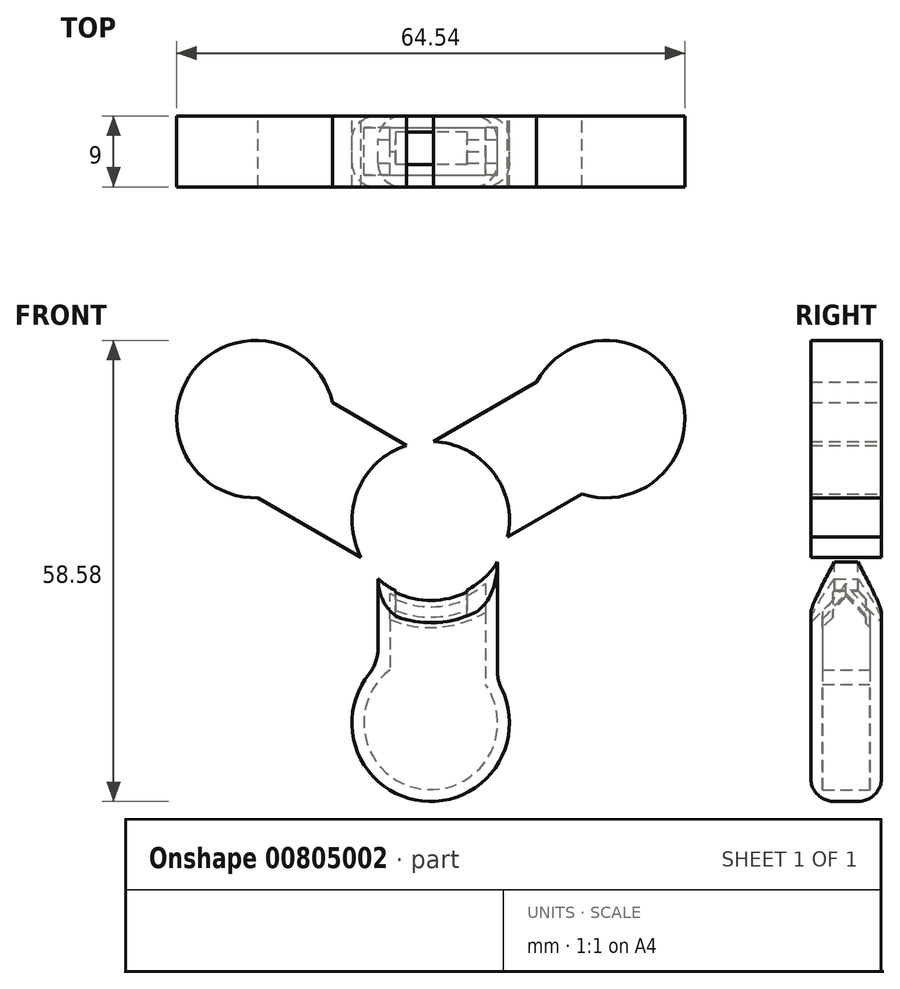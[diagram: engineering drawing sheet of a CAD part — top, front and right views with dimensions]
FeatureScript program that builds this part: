
annotation { "Feature Type Name" : "Feature", "Feature Type Description" : "" }
export const myFeature = defineFeature(function(context is Context, id is Id, definition is map)
    precondition{}
    {
        {
            var Q0;
            Q0=qCreatedBy(makeId("Front.planeOp"),FACE);
            var sketch = newSketch(context, id + "F0", { "sketchPlane" : qUnion([Q0])});
            skCircle(sketch, "E0", {"center": v(0, 0) * mm, "radius": 10 * mm});
            skLineSegment(sketch, "E1", {"start": v(0, 0) * mm, "end": v(0, -10) * mm});
            skLineSegment(sketch, "E2", {"start": v(0, 0) * mm, "end": v(-6.7, -4.19) * mm});
            skLineSegment(sketch, "E3", {"start": v(0, 0) * mm, "end": v(8.48, -5.3) * mm});
            skLineSegment(sketch, "E4.top", {"start": v(-6.63, -33.2) * mm, "end": v(-6.7, -33.2) * mm});
            skLineSegment(sketch, "E4.left", {"start": v(8.48, -5.3) * mm, "end": v(8.48, -20.42) * mm});
            skLineSegment(sketch, "E4.right", {"start": v(-6.7, -5.3) * mm, "end": v(-6.7, -18.3) * mm});
            skArc(sketch, "E5", {"start": v(-6.7, -18.3) * mm, "mid": v(-1.39, -35.62) * mm, "end": v(8.48, -20.42) * mm});
            skLineSegment(sketch, "E6.trimOffspring", {"start": v(-6.7, -33.14) * mm, "end": v(-6.7, -33.2) * mm});
            skLineSegment(sketch, "E7.trimOffspring", {"start": v(-6.7, -5.3) * mm, "end": v(-8.48, -5.3) * mm});
            skSolve(sketch);
        }
        {
            var Q0;
            {var subQ0=sQuery(id+"F0.wireOp",EDGE,"E4.left");Q0=makeQuery(id+"F0.imprint","IMPRINT",FACE,{"disambiguationData":[TD([[makeQuery(id+"F0.imprint","IMPRINT",EDGE,{"derivedFrom":subQ0}),-1.0]])]});}
            extrude(context, id + "F1", {"entities" : qUnion([Q0]), "depth" : 9 * mm, "offsetDistance" : 25 * mm});
        }
        {
            var Q0;
            Q0=qCreatedBy(makeId("Right.planeOp"),FACE);
            var sketch = newSketch(context, id + "F2", { "sketchPlane" : qUnion([Q0])});
            skLineSegment(sketch, "E8", {"start": v(0, 0) * mm, "end": v(-32.6, 0) * mm});
            skSolve(sketch);
        }
        {
            var Q0;
            Q0=makeQuery(id+"F1.opExtrude","SWEPT_BODY",BODY,{"disambiguationData":[OSD([sQuery(id+"F0.wireOp",EDGE,"E0"),sQuery(id+"F0.wireOp",EDGE,"E2"),sQuery(id+"F0.wireOp",EDGE,"E4.left"),sQuery(id+"F0.wireOp",EDGE,"E4.right"),sQuery(id+"F0.wireOp",EDGE,"E5")])]});
            var Q1;
            Q1=sQuery(id+"F2.wireOp",EDGE,"E8");
            circularPattern(context, id + "F3", {"entities" : qUnion([Q0]), "axis" : qUnion([Q1]), "angle" : 360 * degree, "instanceCount" : 3, "equalSpace" : true});
        }
        {
            var Q0;
            Q0=makeQuery(id+"F1.opExtrude","CAP_EDGE",EDGE,{"disambiguationData":[OSD([sQuery(id+"F0.wireOp",EDGE,"E0")])],"isStart":true});
            var Q1;
            Q1=makeQuery(id+"F1.opExtrude","CAP_EDGE",EDGE,{"disambiguationData":[OSD([sQuery(id+"F0.wireOp",EDGE,"E0")])],"isStart":false});
            chamfer(context, id + "F4", {"entities" : qUnion([Q0, Q1]), "width" : 3 * mm, "tangentPropagation" : true});
        }
        {
            var Q0;
            Q0=makeQuery(id+"F1.opExtrude","SWEPT_FACE",FACE,{"disambiguationData":[OSD([sQuery(id+"F0.wireOp",EDGE,"E0")])]});
            shell(context, id + "F5", {"entities" : qUnion([Q0]), "thickness" : 1.5 * mm});
        }
        {
            var Q0;
            Q0=makeQuery(id+"F1.opExtrude","SWEPT_EDGE",EDGE,{"disambiguationData":[OSD([sQuery(id+"F0.wireOp",EDGE,"E4.right"),sQuery(id+"F0.wireOp",EDGE,"E5")])]});
            var Q1;
            Q1=makeQuery(id+"F1.opExtrude","SWEPT_EDGE",EDGE,{"disambiguationData":[OSD([sQuery(id+"F0.wireOp",EDGE,"E4.left"),sQuery(id+"F0.wireOp",EDGE,"E5")])]});
            fillet(context, id + "F6", {"entities" : qUnion([Q0, Q1]), "radius" : 5 * mm, "tangentPropagation" : true, "allowEdgeOverflow" : false});
        }
        {
            var Q0;
            Q0=makeQuery(id+"F1.opExtrude","CAP_EDGE",EDGE,{"disambiguationData":[OSD([sQuery(id+"F0.wireOp",EDGE,"E5")])],"isStart":false});
            var Q1;
            Q1=makeQuery(id+"F1.opExtrude","CAP_EDGE",EDGE,{"disambiguationData":[OSD([sQuery(id+"F0.wireOp",EDGE,"E5")])],"isStart":true});
            fillet(context, id + "F7", {"entities" : qUnion([Q0, Q1]), "radius" : 3 * mm, "tangentPropagation" : true, "allowEdgeOverflow" : false});
        }
        {
            var Q0;
            Q0=qCreatedBy(makeId("Top.planeOp"),FACE);
            var sketch = newSketch(context, id + "F8", { "sketchPlane" : qUnion([Q0])});
            skLineSegment(sketch, "E9.bottom", {"start": v(-4.45, -6.19) * mm, "end": v(4.62, -6.19) * mm});
            skLineSegment(sketch, "E9.top", {"start": v(-4.45, -2.01) * mm, "end": v(4.62, -2.01) * mm});
            skLineSegment(sketch, "E9.left", {"start": v(-4.45, -6.19) * mm, "end": v(-4.45, -2.01) * mm});
            skLineSegment(sketch, "E9.right", {"start": v(4.62, -6.19) * mm, "end": v(4.62, -2.01) * mm});
            skSolve(sketch);
        }
        {
            var Q0;
            Q0=makeQuery(id+"F8.imprint","IMPRINT",FACE,{"disambiguationData":[TD([[makeQuery(id+"F8.imprint","IMPRINT",EDGE,{"derivedFrom":sQuery(id+"F8.wireOp",EDGE,"E9.bottom")}),1.0]])]});
            extrude(context, id + "F9", {"entities" : qUnion([Q0]), "depth" : 25 * mm, "offsetDistance" : 25 * mm});
        }
        {
            var Q0;
            Q0=makeQuery(id+"F9.opExtrude","SWEPT_BODY",BODY,{"disambiguationData":[OSD([sQuery(id+"F8.wireOp",EDGE,"E9.bottom"),sQuery(id+"F8.wireOp",EDGE,"E9.top"),sQuery(id+"F8.wireOp",EDGE,"E9.left"),sQuery(id+"F8.wireOp",EDGE,"E9.right")])]});
            transform(context, id + "F10", {"entities" : qUnion([Q0]), "transformType" : TransformType.TRANSLATION_3D, "dx" : 0 * mm, "dy" : 0 * mm, "dz" : -29.1 * mm, "makeCopy" : false});
        }
        {
            var Q0;
            Q0=makeQuery(id+"F9.opExtrude","SWEPT_BODY",BODY,{"disambiguationData":[OSD([sQuery(id+"F8.wireOp",EDGE,"E9.bottom"),sQuery(id+"F8.wireOp",EDGE,"E9.top"),sQuery(id+"F8.wireOp",EDGE,"E9.left"),sQuery(id+"F8.wireOp",EDGE,"E9.right")])]});
            var Q1;
            Q1=makeQuery(id+"F1.opExtrude","SWEPT_BODY",BODY,{"disambiguationData":[OSD([sQuery(id+"F0.wireOp",EDGE,"E0"),sQuery(id+"F0.wireOp",EDGE,"E4.left"),sQuery(id+"F0.wireOp",EDGE,"E4.right"),sQuery(id+"F0.wireOp",EDGE,"E5")])]});
            booleanBodies(context, id + "F11", {"operationType" : BooleanOperationType.SUBTRACTION, "tools" : qUnion([Q0]), "targets" : qUnion([Q1])});
        }
    });
